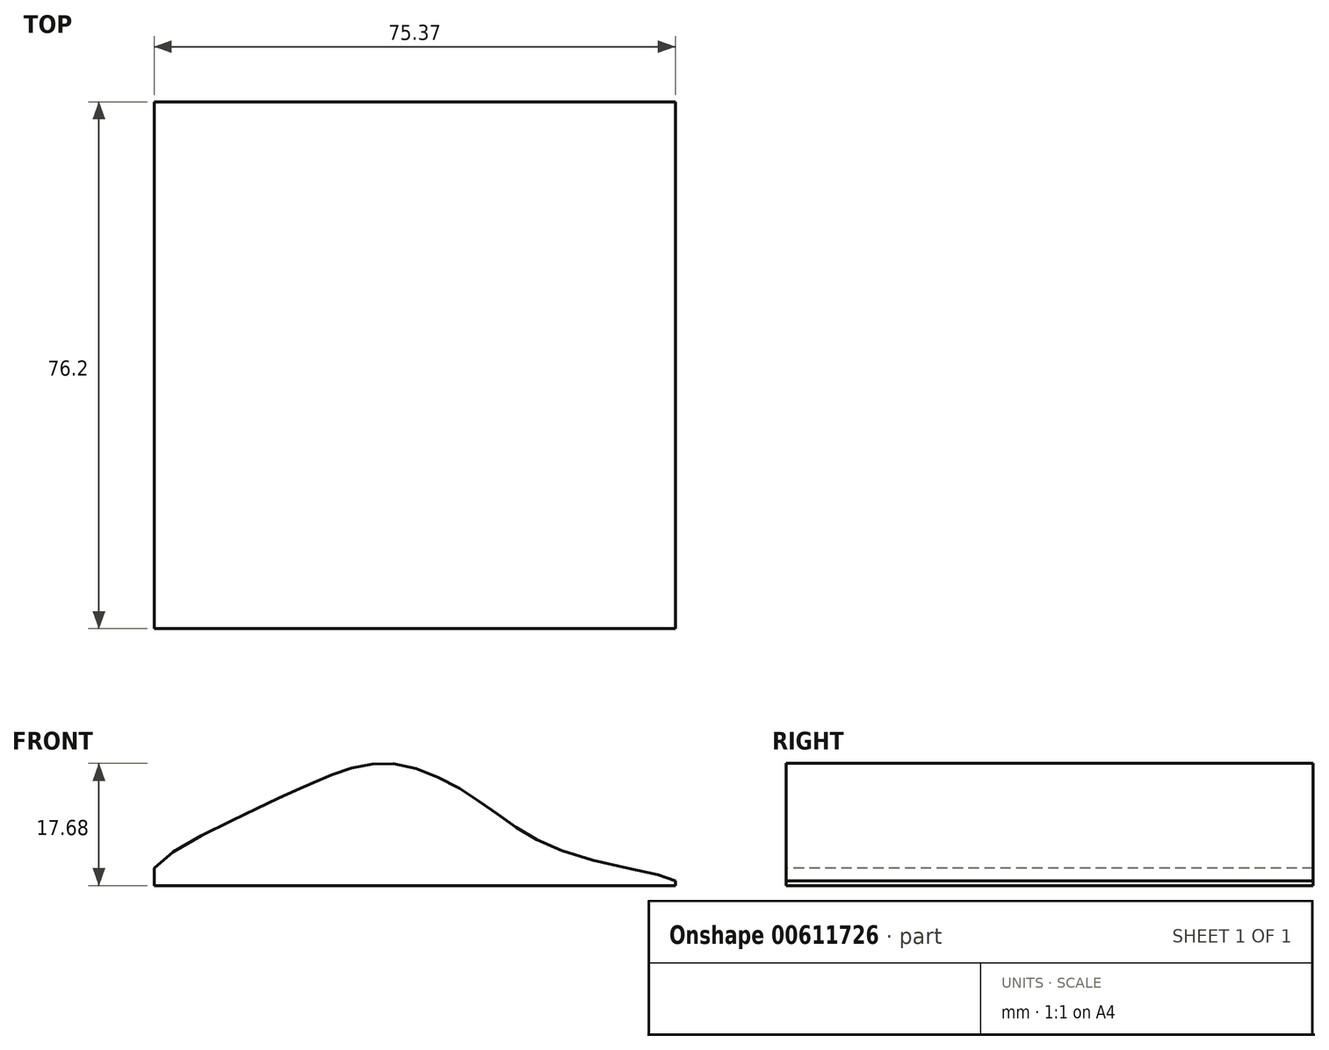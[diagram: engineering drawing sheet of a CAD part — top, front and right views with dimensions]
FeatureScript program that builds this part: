
annotation { "Feature Type Name" : "Feature", "Feature Type Description" : "" }
export const myFeature = defineFeature(function(context is Context, id is Id, definition is map)
    precondition{}
    {
        {
            var Q0;
            Q0=qCreatedBy(makeId("Front.planeOp"),FACE);
            var sketch = newSketch(context, id + "F0", { "sketchPlane" : qUnion([Q0])});
            skLineSegment(sketch, "E0.bottom", {"start": v(0, 0) * mm, "end": v(75.37, 0) * mm});
            skLineSegment(sketch, "E0.top", {"start": v(0, 28.68) * mm, "end": v(75.37, 28.68) * mm});
            skLineSegment(sketch, "E0.left", {"start": v(0, 0) * mm, "end": v(0, 28.68) * mm});
            skLineSegment(sketch, "E0.right", {"start": v(75.37, 0) * mm, "end": v(75.37, 28.68) * mm});
            skSolve(sketch);
        }
        {
            var Q0;
            Q0=makeQuery(id+"F0.imprint","IMPRINT",FACE,{"disambiguationData":[TD([[makeQuery(id+"F0.imprint","IMPRINT",EDGE,{"derivedFrom":sQuery(id+"F0.wireOp",EDGE,"E0.bottom")}),1.0]])]});
            extrude(context, id + "F1", {"entities" : qUnion([Q0]), "depth" : 76.2 * mm, "offsetDistance" : 25.4 * mm});
        }
        {
            var Q0;
            Q0=makeQuery(id+"F1.opExtrude","CAP_FACE",FACE,{"disambiguationData":[OSD([sQuery(id+"F0.wireOp",EDGE,"E0.bottom"),sQuery(id+"F0.wireOp",EDGE,"E0.top"),sQuery(id+"F0.wireOp",EDGE,"E0.left"),sQuery(id+"F0.wireOp",EDGE,"E0.right")])],"isStart":false});
            var sketch = newSketch(context, id + "F2", { "sketchPlane" : qUnion([Q0])});
            skFitSpline(sketch, "E1", {"points": [v(0, 0) * mm, v(11.6, 9.58) * mm, v(23.42, 15.06) * mm, v(34.08, 17.65) * mm, v(47.05, 12.18) * mm, v(60.89, 4.4) * mm, v(75.37, 0) * mm, v(0, 0) * mm]});
            skSolve(sketch);
        }
        {
            var Q0;
            {var subQ5=makeQuery(id+"F1.opExtrude","CAP_EDGE",EDGE,{"disambiguationData":[OSD([sQuery(id+"F0.wireOp",EDGE,"E0.top")])],"isStart":false});Q0=makeQuery(id+"F2.imprint","IMPRINT",FACE,{"disambiguationData":[TD([[makeQuery(id+"F2.imprint","IMPRINT",EDGE,{"derivedFrom":subQ5}),-1.0]])]});}
            extrude(context, id + "F3", {"entities" : qUnion([Q0]), "operationType" : NewBodyOperationType.REMOVE, "oppositeDirection" : true, "depth" : 152.4 * mm, "offsetDistance" : 25.4 * mm});
        }
    });
